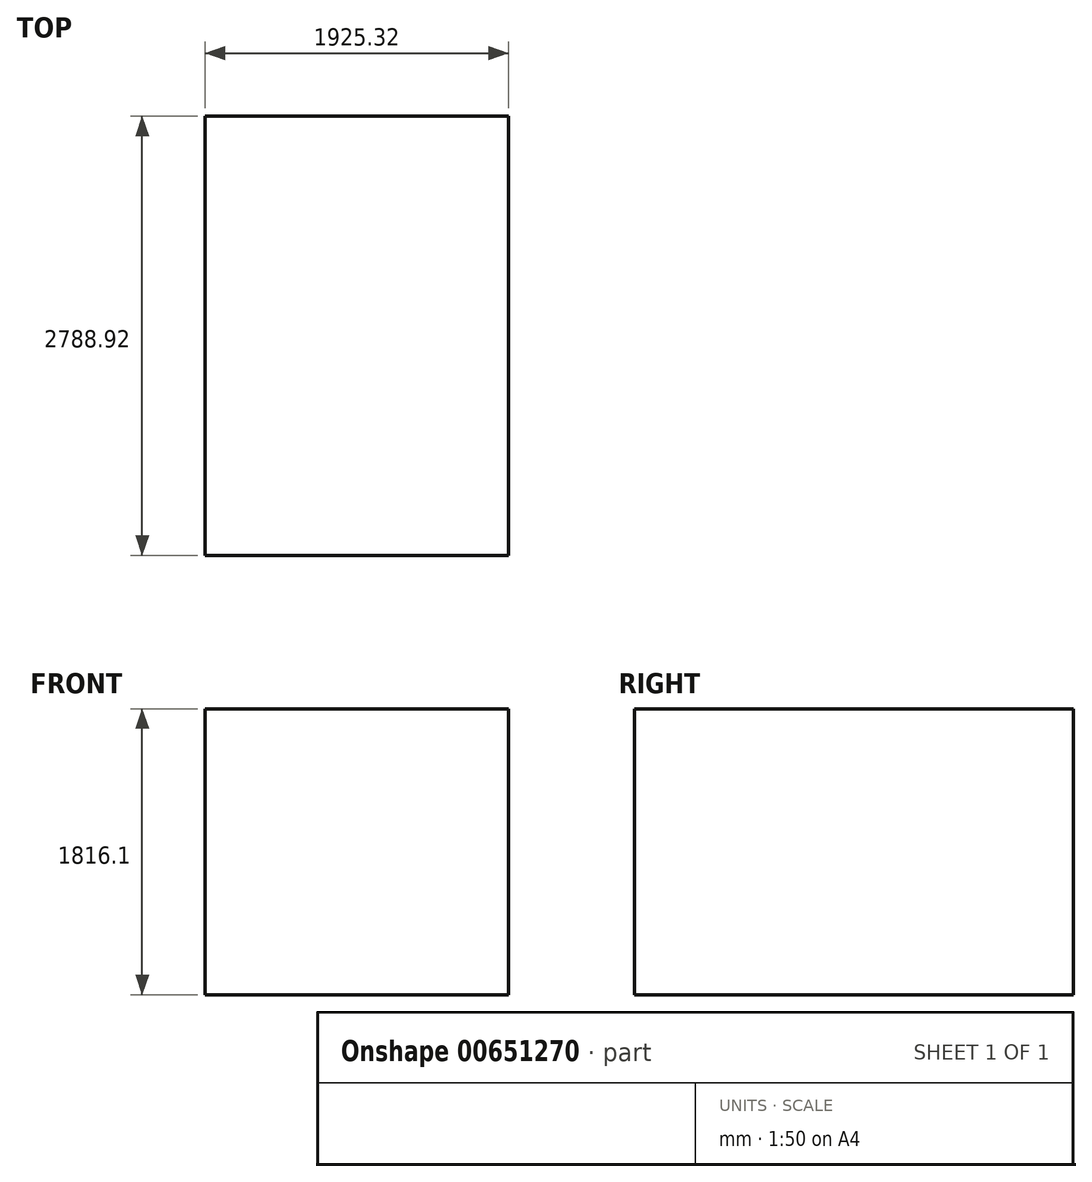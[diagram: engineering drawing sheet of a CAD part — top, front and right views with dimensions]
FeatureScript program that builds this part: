
annotation { "Feature Type Name" : "Feature", "Feature Type Description" : "" }
export const myFeature = defineFeature(function(context is Context, id is Id, definition is map)
    precondition{}
    {
        {
            var Q0;
            Q0=qCreatedBy(makeId("Front.planeOp"),FACE);
            var sketch = newSketch(context, id + "F0", { "sketchPlane" : qUnion([Q0])});
            skLineSegment(sketch, "E0.bottom", {"start": v(-962.66, 1816.1) * mm, "end": v(962.66, 1816.1) * mm});
            skLineSegment(sketch, "E0.top", {"start": v(-962.66, 0) * mm, "end": v(962.66, 0) * mm});
            skLineSegment(sketch, "E0.left", {"start": v(-962.66, 1816.1) * mm, "end": v(-962.66, 0) * mm});
            skLineSegment(sketch, "E0.right", {"start": v(962.66, 1816.1) * mm, "end": v(962.66, 0) * mm});
            skLineSegment(sketch, "E1", {"start": v(0, 0) * mm, "end": v(0, 2531.92) * mm, "construction": true});
            skSolve(sketch);
        }
        {
            var Q0;
            Q0=makeQuery(id+"F0.imprint","IMPRINT",FACE,{"disambiguationData":[TD([[makeQuery(id+"F0.imprint","IMPRINT",EDGE,{"derivedFrom":sQuery(id+"F0.wireOp",EDGE,"E0.bottom")}),-1.0]])]});
            extrude(context, id + "F1", {"entities" : qUnion([Q0]), "depth" : 2788.92 * mm, "offsetDistance" : 25.4 * mm});
        }
    });
